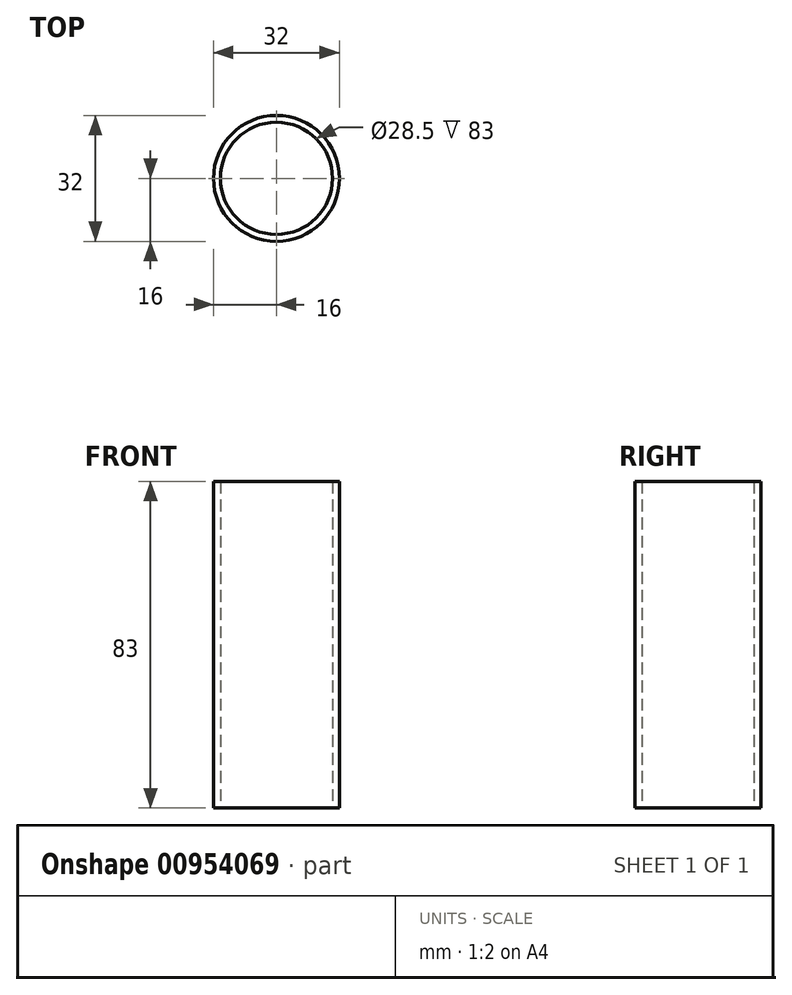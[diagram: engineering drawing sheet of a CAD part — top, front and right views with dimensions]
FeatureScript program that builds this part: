
annotation { "Feature Type Name" : "Feature", "Feature Type Description" : "" }
export const myFeature = defineFeature(function(context is Context, id is Id, definition is map)
    precondition{}
    {
        {
            var Q0;
            Q0=qCreatedBy(makeId("Top.planeOp"),FACE);
            var sketch = newSketch(context, id + "F0", { "sketchPlane" : qUnion([Q0])});
            skCircle(sketch, "E0", {"center": v(0, 0) * mm, "radius": 14.25 * mm});
            skCircle(sketch, "E1", {"center": v(0, 0) * mm, "radius": 16 * mm});
            skLineSegment(sketch, "E2", {"start": v(-11, 11.62) * mm, "end": v(-11, 76.62) * mm});
            skLineSegment(sketch, "E3", {"start": v(11, 11.62) * mm, "end": v(11, 76.62) * mm});
            skArc(sketch, "E4", {"start": v(-10.2, 80.74) * mm, "mid": v(0, 65.62) * mm, "end": v(10.2, 80.74) * mm});
            skLineSegment(sketch, "E5", {"start": v(-10.2, 80.74) * mm, "end": v(10.2, 80.74) * mm});
            skArc(sketch, "E6", {"start": v(-8, 80.74) * mm, "mid": v(0, 67.62) * mm, "end": v(8, 80.74) * mm});
            skSolve(sketch);
        }
        {
            var Q0;
            {var subQ0=sQuery(id+"F0.wireOp",EDGE,"E2");Q0=makeQuery(id+"F0.imprint","IMPRINT",FACE,{"disambiguationData":[TD([[makeQuery(id+"F0.imprint","IMPRINT",EDGE,{"derivedFrom":subQ0}),-1.0]])]});}
            var Q1;
            Q1=makeQuery(id+"F0.imprint","IMPRINT",FACE,{"disambiguationData":[TD([[makeQuery(id+"F0.imprint","IMPRINT",EDGE,{"derivedFrom":sQuery(id+"F0.wireOp",EDGE,"E0")}),-1.0]])]});
            extrude(context, id + "F1", {"entities" : qUnion([Q0, Q1]), "endBound" : BoundingType.SYMMETRIC, "depth" : 83 * mm, "offsetDistance" : 25 * mm});
        }
    });
